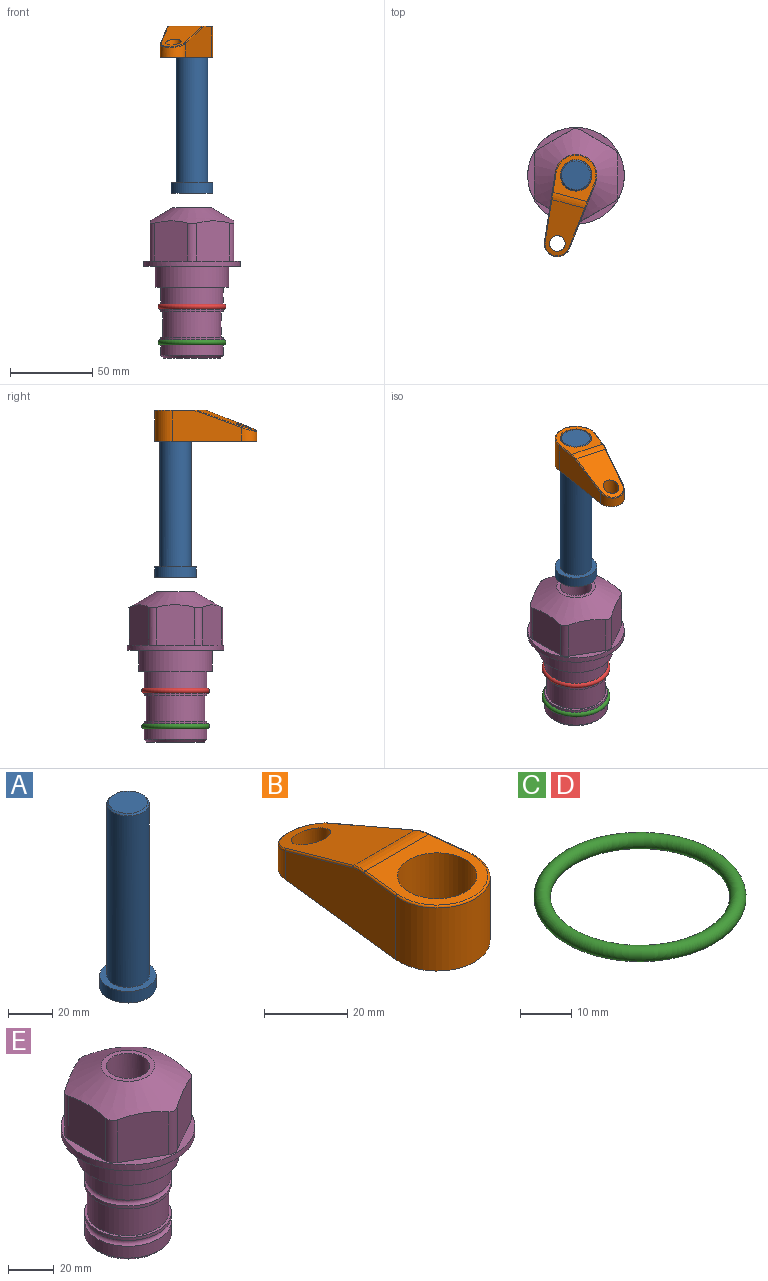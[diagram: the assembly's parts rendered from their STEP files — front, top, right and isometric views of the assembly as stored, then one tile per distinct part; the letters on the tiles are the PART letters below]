
ASSEMBLY  parts=5 mates=3
PART A: 6 faces, bbox 25.4x25.4x101.6 mm
  f0: plane 17.46x17.46mm, normal (0,0,1), area 239.5mm2, adj f5
  f1: plane 25.4x25.4mm, normal (0,0,-1), area 506.7mm2, adj f2
  f2: cylinder r=12.7mm len=25.4mm, axis (0,0,1), area 506.7mm2, adj f1,f3
  f3: plane 25.4x25.4mm, normal (0,0,1), area 221.7mm2, adj f2,f4
  f4: cylinder r=9.53mm len=94.46mm, axis (0,0,1), area 5653mm2, adj f3,f5
  f5: cone r=8.73mm half-angle=45deg, axis (0,0,-1), area 64.4mm2, adj f0,f4
PART B: 44 faces, bbox 27.5x64.5x19.1 mm
  f0: plane 2.3x0.95mm, normal (0,0,-1), area 1mm2, adj f25,f30,f34
  f1: plane 63.5x25.4mm, normal (0,0,-1), area 561.7mm2, adj f2,f3,f4,f5,f6,f7,f19,f20
  f2: cylinder r=12.7mm len=25.4mm, axis (0,0,-1), area 792.2mm2, adj f1,f3,f5,f13
  f3: plane 42.33x18.54mm, normal (0.99,0.11,0), area 647mm2, adj f1,f2,f4,f11,f12,f14
  f4: cylinder r=7.94mm len=15.78mm, axis (0,0,-1), area 158.6mm2, adj f1,f3,f5,f16
  f5: plane 42.33x18.54mm, normal (-0.99,0.11,0), area 647mm2, adj f1,f2,f4,f15,f17,f18
  f6: cylinder r=9.53mm len=19.05mm, axis (0,0,-1), area 1140.1mm2, adj f1,f8
  f7: cylinder r=4.76mm len=10.98mm, axis (0,0,-1), area 276.1mm2, adj f1,f9
  f8: plane 25.83x24.38mm, normal (0,0,1), area 262.2mm2, adj f6,f10,f11,f13,f15
  f9: plane 32.49x20.55mm, normal (0,0.34,0.94), area 489.9mm2, adj f7,f10,f14,f16,f18
  f10: cylinder r=12.7mm len=21.49mm, axis (-1,0,0), area 93.2mm2, adj f8,f9,f12,f17
  f11: cylinder r=0.51mm len=12.34mm, axis (0.11,-0.99,0), area 9.9mm2, adj f3,f8,f12,f13
  f12: bspline ~7.62x1.64mm, area 3.5mm2, adj f3,f10,f11,f14
  f13: torus R=12.19mm, axis (0,0,1), area 33.6mm2, adj f2,f8,f11,f15
  f14: cylinder r=0.51mm len=26.01mm, axis (0.1,-0.93,0.34), area 21.6mm2, adj f3,f9,f12,f16
  f15: cylinder r=0.51mm len=12.34mm, axis (0.11,0.99,0), area 9.9mm2, adj f5,f8,f13,f17
  f16: bspline ~15.78x7.05mm, area 15.7mm2, adj f4,f9,f14,f18
  f17: bspline ~7.62x1.64mm, area 3.5mm2, adj f5,f10,f15,f18
  f18: cylinder r=0.51mm len=26.01mm, axis (0.1,0.93,-0.34), area 21.6mm2, adj f5,f9,f16,f17
  f19: plane 21.6x14.29mm, normal (-0.99,-0.11,0), area 242.6mm2, adj f1,f26,f28,f34,f36,f38
  f20: plane 21.6x14.29mm, normal (0.99,-0.11,0), area 242.6mm2, adj f1,f27,f29,f37,f39,f41
  f21: cylinder r=12.7mm len=14.29mm, axis (0,0,-1), area 173.2mm2, adj f1,f26,f27,f30,f31,f33
  f22: cylinder r=7.94mm len=7.63mm, axis (0,0,-1), area 53.8mm2, adj f1,f28,f29,f42
  f23: plane 2.3x0.95mm, normal (0,0,-1), area 1mm2, adj f25,f33,f37
  f24: plane 17.94x12.32mm, normal (0,-0.34,-0.94), area 191.2mm2, adj f25,f38,f41,f42
  f25: cylinder r=9.53mm len=12.93mm, axis (-1,0,0), area 37.5mm2, adj f0,f23,f24,f31,f36,f39
  f26: cylinder r=1.59mm len=14.29mm, axis (0,0,-1), area 49mm2, adj f1,f19,f21,f32
  f27: cylinder r=1.59mm len=14.29mm, axis (0,0,-1), area 49mm2, adj f1,f20,f21,f35
  f28: cylinder r=1.59mm len=7.28mm, axis (0,0,-1), area 22.1mm2, adj f1,f19,f22,f40
  f29: cylinder r=1.59mm len=7.28mm, axis (0,0,-1), area 22.1mm2, adj f1,f20,f22,f43
  f30: torus R=14.29mm, axis (0,0,1), area 5.8mm2, adj f0,f21,f31,f32
  f31: bspline ~11.06x2.73mm, area 20.8mm2, adj f21,f25,f30,f33
  f32: sphere r=1.59mm, area 5.4mm2, adj f26,f30,f34
  f33: torus R=14.29mm, axis (0,0,1), area 5.8mm2, adj f21,f23,f31,f35
  f34: cylinder r=1.59mm len=1.68mm, axis (-0.11,0.99,0), area 2.4mm2, adj f0,f19,f32,f36
  f35: sphere r=1.59mm, area 5.4mm2, adj f27,f33,f37
  f36: bspline ~5.82x2.33mm, area 7.7mm2, adj f19,f25,f34,f38
  f37: cylinder r=1.59mm len=1.68mm, axis (0.11,0.99,0), area 2.4mm2, adj f20,f23,f35,f39
  f38: cylinder r=1.59mm len=18.33mm, axis (0.1,-0.93,0.34), area 46.7mm2, adj f19,f24,f36,f40
  f39: bspline ~5.82x2.33mm, area 7.7mm2, adj f20,f25,f37,f41
  f40: sphere r=1.59mm, area 3.6mm2, adj f28,f38,f42
  f41: cylinder r=1.59mm len=18.33mm, axis (0.1,0.93,-0.34), area 46.7mm2, adj f20,f24,f39,f43
  f42: bspline ~8.31x1.84mm, area 15.3mm2, adj f22,f24,f40,f43
  f43: sphere r=1.59mm, area 3.6mm2, adj f29,f41,f42
PART C: 1 faces, bbox 44.7x44.7x3.2 mm
  f0: torus R=19.05mm, axis (0,0,1), area 1193.9mm2
PART D: same geometry as C
PART E: 36 faces, bbox 58.7x58.7x91.2 mm
  f0: cylinder r=17.78mm len=35.56mm, axis (0,0,1), area 1670.8mm2, adj f23,f24,f31
  f1: cylinder r=19.05mm len=38.1mm, axis (0,0,1), area 1191.9mm2, adj f26,f27,f30
  f2: plane 58.66x58.66mm, normal (0,0,-1), area 1150.6mm2, adj f3,f28
  f3: cylinder r=29.33mm len=58.66mm, axis (0,0,-1), area 585.1mm2, adj f2,f4
  f4: plane 58.66x58.66mm, normal (0,0,1), area 475.9mm2, adj f3,f5,f6,f7,f8,f9,f10,f11
  f5: plane 24.5x20.32mm, normal (-0.5,0.87,0), area 562.8mm2, adj f4,f15,f16,f17
  f6: plane 24.5x20.32mm, normal (0.5,0.87,0), area 562.8mm2, adj f4,f14,f15,f17
  f7: plane 24.5x23.48mm, normal (1,0,0), area 562.8mm2, adj f4,f13,f14,f17
  f8: plane 24.5x20.32mm, normal (0.5,-0.87,0), area 562.8mm2, adj f4,f12,f13,f17
  f9: plane 24.5x20.32mm, normal (-0.5,-0.87,0), area 562.8mm2, adj f4,f11,f12,f17
  f10: plane 24.5x23.48mm, normal (-1,0,0), area 562.8mm2, adj f4,f11,f16,f17
  f11: cylinder r=5.08mm len=23.01mm, axis (0,0,-1), area 121.2mm2, adj f4,f9,f10,f17
  f12: cylinder r=5.08mm len=23.01mm, axis (0,0,-1), area 121.2mm2, adj f4,f8,f9,f17
  f13: cylinder r=5.08mm len=23.01mm, axis (0,0,-1), area 121.2mm2, adj f4,f7,f8,f17
  f14: cylinder r=5.08mm len=23.01mm, axis (0,0,-1), area 121.2mm2, adj f4,f6,f7,f17
  f15: cylinder r=5.08mm len=23.01mm, axis (0,0,-1), area 121.2mm2, adj f4,f5,f6,f17
  f16: cylinder r=5.08mm len=23.01mm, axis (0,0,-1), area 121.2mm2, adj f4,f5,f10,f17
  f17: cone r=11.73mm half-angle=60deg, axis (0,0,-1), area 2071.8mm2, adj f5,f6,f7,f8,f9,f10,f11,f12
  f18: plane 23.46x23.46mm, normal (0,0,1), area 147.4mm2, adj f17,f35
  f19: plane 34.93x34.93mm, normal (0,0,-1), area 958mm2, adj f29
  f20: cylinder r=19.05mm len=38.1mm, axis (0,0,1), area 760.1mm2, adj f21,f29
  f21: torus R=19.05mm, axis (0,0,1), area 565.3mm2, adj f20,f22
  f22: cylinder r=19.05mm len=38.1mm, axis (0,0,1), area 190mm2, adj f21,f23
  f23: plane 38.1x38.1mm, normal (0,0,1), area 146.9mm2, adj f0,f22
  f24: plane 38.1x38.1mm, normal (0,0,-1), area 146.9mm2, adj f0,f25
  f25: cylinder r=19.05mm len=38.1mm, axis (0,0,1), area 190mm2, adj f24,f26
  f26: torus R=19.05mm, axis (0,0,1), area 565.3mm2, adj f1,f25
  f27: plane 44.45x44.45mm, normal (0,0,-1), area 411.7mm2, adj f1,f28
  f28: cylinder r=22.23mm len=44.45mm, axis (0,0,1), area 1773.5mm2, adj f2,f27
  f29: cone r=19.05mm half-angle=45deg, axis (0,0,1), area 257.5mm2, adj f19,f20
  f30: cylinder r=3.17mm len=6.75mm, axis (-1,0,0), area 128mm2, adj f1,f33
  f31: cylinder r=3.17mm len=6.35mm, axis (-1,0,0), area 102.5mm2, adj f0,f33
  f32: plane 25.4x25.4mm, normal (0,0,1), area 506.7mm2, adj f33
  f33: cylinder r=12.7mm len=66.42mm, axis (0,0,-1), area 5236.2mm2, adj f30,f31,f32,f34
  f34: cone r=9.53mm half-angle=30deg, axis (0,0,-1), area 443.4mm2, adj f33,f35
  f35: cylinder r=9.53mm len=19.05mm, axis (0,0,-1), area 849mm2, adj f18,f34
PLACE A rot(axis=(0,0,-1),105.3deg) t=(0,0,72.24)mm
PLACE B rot(axis=(0,0,1),164.7deg) t=(0,0,126.85)mm
PLACE C t=(0,0,-21.59)mm
PLACE D at identity
PLACE E at identity fixed
MATE fastened C.f0 <-> E.f0  axis (0,0,1) through (0,0,-46.1)mm
MATE cylindrical A.f2 <-> E.f0  axis (0,0,1) through (0,0,97.88)mm
MATE fastened B.f2 <-> A.f2  axis (0,0,1) through (0,0,145.9)mm
